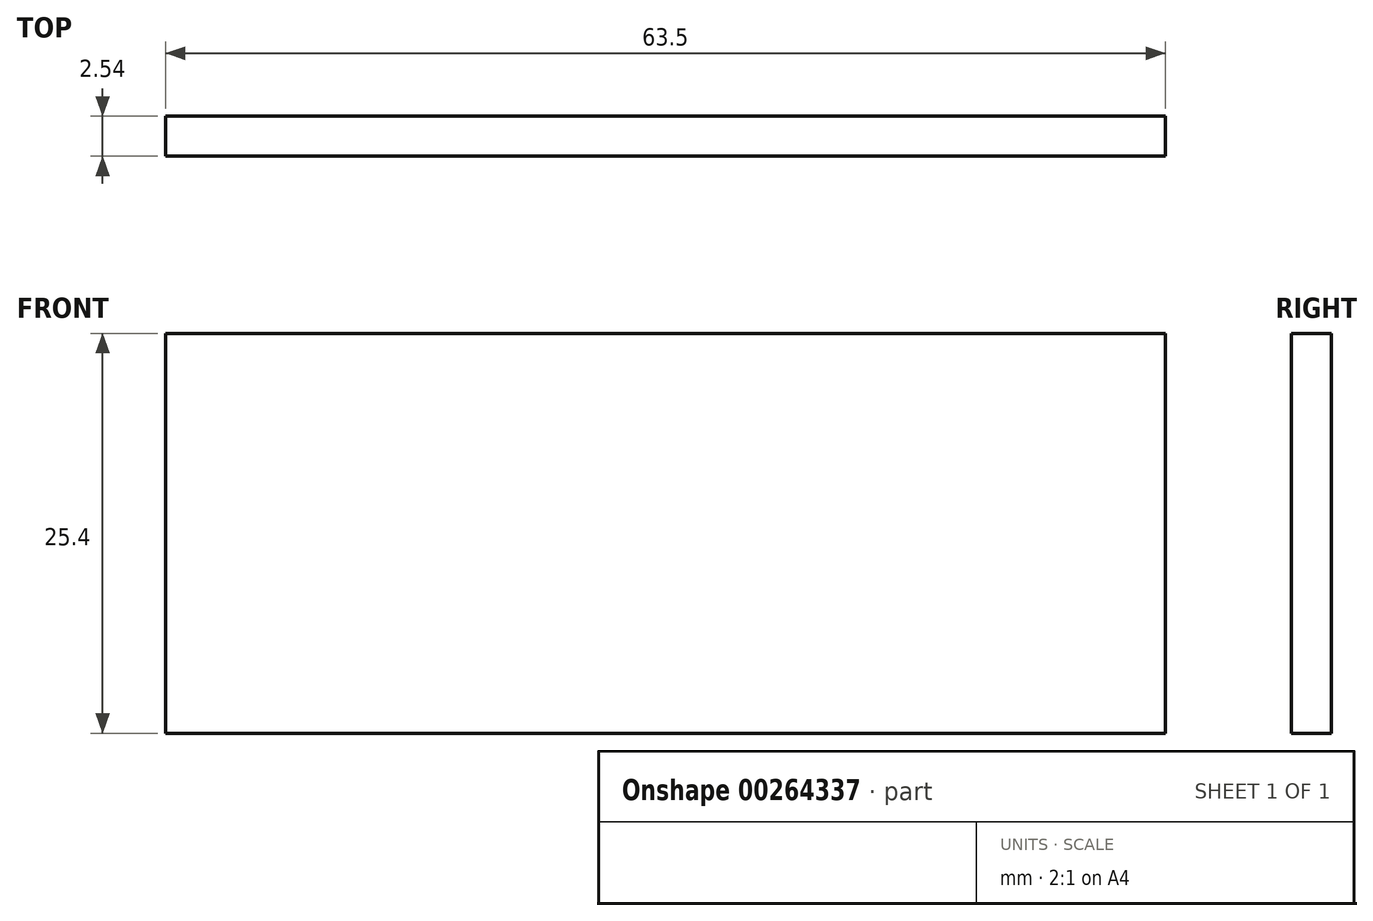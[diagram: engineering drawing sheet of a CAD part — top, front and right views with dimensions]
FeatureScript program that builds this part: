
annotation { "Feature Type Name" : "Feature", "Feature Type Description" : "" }
export const myFeature = defineFeature(function(context is Context, id is Id, definition is map)
    precondition{}
    {
        {
            var Q0;
            Q0=qCreatedBy(makeId("Front.planeOp"),FACE);
            var sketch = newSketch(context, id + "F0", { "sketchPlane" : qUnion([Q0])});
            skLineSegment(sketch, "E0.bottom", {"start": v(31.75, -12.7) * mm, "end": v(-31.75, -12.7) * mm});
            skLineSegment(sketch, "E0.top", {"start": v(31.75, 12.7) * mm, "end": v(-31.75, 12.7) * mm});
            skLineSegment(sketch, "E0.left", {"start": v(31.75, -12.7) * mm, "end": v(31.75, 12.7) * mm});
            skLineSegment(sketch, "E0.right", {"start": v(-31.75, -12.7) * mm, "end": v(-31.75, 12.7) * mm});
            skPoint(sketch, "E0.middle", {"position": v(0, 0) * mm});
            skSolve(sketch);
        }
        {
            var Q0;
            Q0 = qSketchRegion(id + "F0", true);
            extrude(context, id + "F1", {"entities" : qUnion([Q0]), "depth" : 2.54 * mm});
        }
    });
